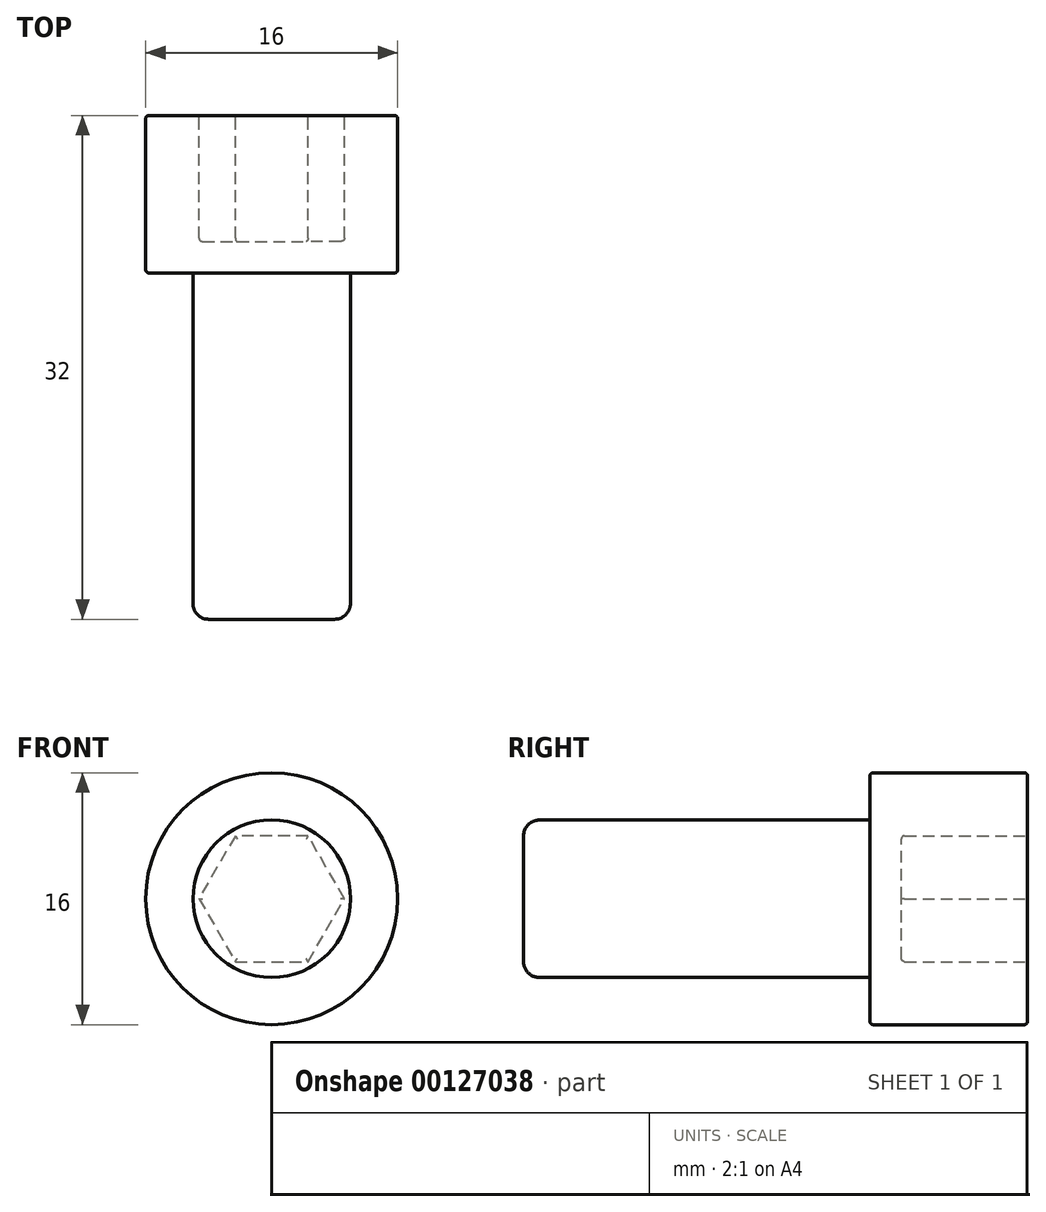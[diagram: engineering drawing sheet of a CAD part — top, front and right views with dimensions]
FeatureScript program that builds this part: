
annotation { "Feature Type Name" : "Feature", "Feature Type Description" : "" }
export const myFeature = defineFeature(function(context is Context, id is Id, definition is map)
    precondition{}
    {
        {
            var Q0;
            Q0=qCreatedBy(makeId("Front.planeOp"),FACE);
            var sketch = newSketch(context, id + "F0", { "sketchPlane" : qUnion([Q0])});
            skCircle(sketch, "E0", {"center": v(0, 0) * mm, "radius": 5 * mm});
            skCircle(sketch, "E1", {"center": v(0, 0) * mm, "radius": 8 * mm});
            skSolve(sketch);
        }
        {
            var Q0;
            Q0=makeQuery(id+"F0.imprint","IMPRINT",FACE,{"disambiguationData":[TD([[makeQuery(id+"F0.imprint","IMPRINT",EDGE,{"derivedFrom":sQuery(id+"F0.wireOp",EDGE,"199a0a2e-5cb0-4f73-b718-4463bf7d904f.0")}),-1.0]])]});
            var Q1;
            Q1=makeQuery(id+"F0.imprint","IMPRINT",FACE,{"disambiguationData":[TD([[makeQuery(id+"F0.imprint","IMPRINT",EDGE,{"derivedFrom":sQuery(id+"F0.wireOp",EDGE,"E0")}),1.0]])]});
            extrude(context, id + "F1", {"entities" : qUnion([Q0, Q1]), "depth" : 22 * mm});
        }
        {
            var Q0;
            Q0=makeQuery(id+"F0.imprint","IMPRINT",FACE,{"disambiguationData":[TD([[makeQuery(id+"F0.imprint","IMPRINT",EDGE,{"derivedFrom":sQuery(id+"F0.wireOp",EDGE,"E0")}),-1.0]])]});
            var Q1;
            Q1=makeQuery(id+"F0.imprint","IMPRINT",FACE,{"disambiguationData":[TD([[makeQuery(id+"F0.imprint","IMPRINT",EDGE,{"derivedFrom":sQuery(id+"F0.wireOp",EDGE,"199a0a2e-5cb0-4f73-b718-4463bf7d904f.0")}),-1.0]])]});
            var Q2;
            Q2=makeQuery(id+"F0.imprint","IMPRINT",FACE,{"disambiguationData":[TD([[makeQuery(id+"F0.imprint","IMPRINT",EDGE,{"derivedFrom":sQuery(id+"F0.wireOp",EDGE,"E0")}),1.0]])]});
            extrude(context, id + "F2", {"entities" : qUnion([Q0, Q1, Q2]), "operationType" : NewBodyOperationType.ADD, "oppositeDirection" : true, "depth" : 10 * mm});
        }
        {
            var Q0;
            Q0=makeQuery(id+"F2.opExtrude","CAP_FACE",FACE,{"disambiguationData":[OSD([sQuery(id+"F0.wireOp",EDGE,"E1")])],"isStart":false});
            var sketch = newSketch(context, id + "F3", { "sketchPlane" : qUnion([Q0])});
            skCircle(sketch, "E2.cCircle", {"center": v(0, 0) * mm, "radius": 4 * mm, "construction": true});
            skLineSegment(sketch, "E2.0", {"start": v(2.3, -4) * mm, "end": v(-2.3, -4) * mm});
            skLineSegment(sketch, "E2.1", {"start": v(-2.3, -4) * mm, "end": v(-4.62, 0) * mm});
            skLineSegment(sketch, "E2.2", {"start": v(-4.62, 0) * mm, "end": v(-2.3, 4) * mm});
            skLineSegment(sketch, "E2.3", {"start": v(-2.3, 4) * mm, "end": v(2.3, 4) * mm});
            skLineSegment(sketch, "E2.4", {"start": v(2.3, 4) * mm, "end": v(4.62, 0) * mm});
            skLineSegment(sketch, "E2.5", {"start": v(4.62, 0) * mm, "end": v(2.3, -4) * mm});
            skPoint(sketch, "E2.0.midPoint", {"position": v(0, -4) * mm});
            skSolve(sketch);
        }
        {
            var Q0;
            Q0=makeQuery(id+"F3.imprint","IMPRINT",FACE,{"disambiguationData":[TD([[makeQuery(id+"F3.imprint","IMPRINT",EDGE,{"derivedFrom":sQuery(id+"F3.wireOp",EDGE,"E2.0")}),-1.0]])]});
            extrude(context, id + "F4", {"entities" : qUnion([Q0]), "operationType" : NewBodyOperationType.REMOVE, "oppositeDirection" : true, "depth" : 8 * mm});
        }
        {
            var Q0;
            Q0=makeQuery(id+"F4.boolean.opBoolean","COPY",EDGE,{"derivedFrom":makeQuery(id+"F4.opExtrude","CAP_EDGE",EDGE,{"disambiguationData":[OSD([sQuery(id+"F3.wireOp",EDGE,"E2.4")])],"isStart":false})});
            var Q1;
            Q1=makeQuery(id+"F4.boolean.opBoolean","COPY",EDGE,{"derivedFrom":makeQuery(id+"F4.opExtrude","CAP_EDGE",EDGE,{"disambiguationData":[OSD([sQuery(id+"F3.wireOp",EDGE,"E2.1")])],"isStart":false})});
            var Q2;
            Q2=makeQuery(id+"F4.boolean.opBoolean","COPY",EDGE,{"derivedFrom":makeQuery(id+"F4.opExtrude","CAP_EDGE",EDGE,{"disambiguationData":[OSD([sQuery(id+"F3.wireOp",EDGE,"E2.3")])],"isStart":false})});
            var Q3;
            Q3=makeQuery(id+"F4.boolean.opBoolean","COPY",EDGE,{"derivedFrom":makeQuery(id+"F4.opExtrude","CAP_EDGE",EDGE,{"disambiguationData":[OSD([sQuery(id+"F3.wireOp",EDGE,"E2.0")])],"isStart":true})});
            var Q4;
            Q4=makeQuery(id+"F4.boolean.opBoolean","COPY",EDGE,{"derivedFrom":makeQuery(id+"F4.opExtrude","CAP_EDGE",EDGE,{"disambiguationData":[OSD([sQuery(id+"F3.wireOp",EDGE,"E2.5")])],"isStart":false})});
            var Q5;
            Q5=makeQuery(id+"F4.boolean.opBoolean","COPY",EDGE,{"derivedFrom":makeQuery(id+"F4.opExtrude","CAP_EDGE",EDGE,{"disambiguationData":[OSD([sQuery(id+"F3.wireOp",EDGE,"E2.0")])],"isStart":false})});
            var Q6;
            Q6=makeQuery(id+"F4.boolean.opBoolean","COPY",EDGE,{"derivedFrom":makeQuery(id+"F4.opExtrude","CAP_EDGE",EDGE,{"disambiguationData":[OSD([sQuery(id+"F3.wireOp",EDGE,"E2.2")])],"isStart":true})});
            var Q7;
            Q7=makeQuery(id+"F4.boolean.opBoolean","COPY",EDGE,{"derivedFrom":makeQuery(id+"F4.opExtrude","CAP_EDGE",EDGE,{"disambiguationData":[OSD([sQuery(id+"F3.wireOp",EDGE,"E2.2")])],"isStart":false})});
            var Q8;
            Q8=makeQuery(id+"F4.boolean.opBoolean","COPY",EDGE,{"derivedFrom":makeQuery(id+"F4.opExtrude","CAP_EDGE",EDGE,{"disambiguationData":[OSD([sQuery(id+"F3.wireOp",EDGE,"E2.5")])],"isStart":true})});
            var Q9;
            Q9=makeQuery(id+"F4.boolean.opBoolean","COPY",EDGE,{"derivedFrom":makeQuery(id+"F4.opExtrude","CAP_EDGE",EDGE,{"disambiguationData":[OSD([sQuery(id+"F3.wireOp",EDGE,"E2.4")])],"isStart":true})});
            var Q10;
            Q10=makeQuery(id+"F2.opExtrude","CAP_EDGE",EDGE,{"disambiguationData":[OSD([sQuery(id+"F0.wireOp",EDGE,"E1")])],"isStart":false});
            var Q11;
            Q11=makeQuery(id+"F4.boolean.opBoolean","COPY",EDGE,{"derivedFrom":makeQuery(id+"F4.opExtrude","CAP_EDGE",EDGE,{"disambiguationData":[OSD([sQuery(id+"F3.wireOp",EDGE,"E2.3")])],"isStart":true})});
            var Q12;
            Q12=makeQuery(id+"F4.boolean.opBoolean","COPY",EDGE,{"derivedFrom":makeQuery(id+"F4.opExtrude","CAP_EDGE",EDGE,{"disambiguationData":[OSD([sQuery(id+"F3.wireOp",EDGE,"E2.1")])],"isStart":true})});
            var Q13;
            Q13=makeQuery(id+"F2.opExtrude","CAP_EDGE",EDGE,{"disambiguationData":[OSD([sQuery(id+"F0.wireOp",EDGE,"E1")])],"isStart":true});
            fillet(context, id + "F5", {"entities" : qUnion([Q0, Q1, Q2, Q3, Q4, Q5, Q6, Q7, Q8, Q9, Q10, Q11, Q12, Q13]), "radius" : .2 * mm, "tangentPropagation" : true, "allowEdgeOverflow" : false});
        }
        {
            var Q0;
            Q0=makeQuery(id+"F1.opExtrude","CAP_EDGE",EDGE,{"disambiguationData":[OSD([sQuery(id+"F0.wireOp",EDGE,"E0")])],"isStart":false});
            fillet(context, id + "F6", {"entities" : qUnion([Q0]), "radius" : 1 * mm, "tangentPropagation" : true, "allowEdgeOverflow" : false});
        }
    });
